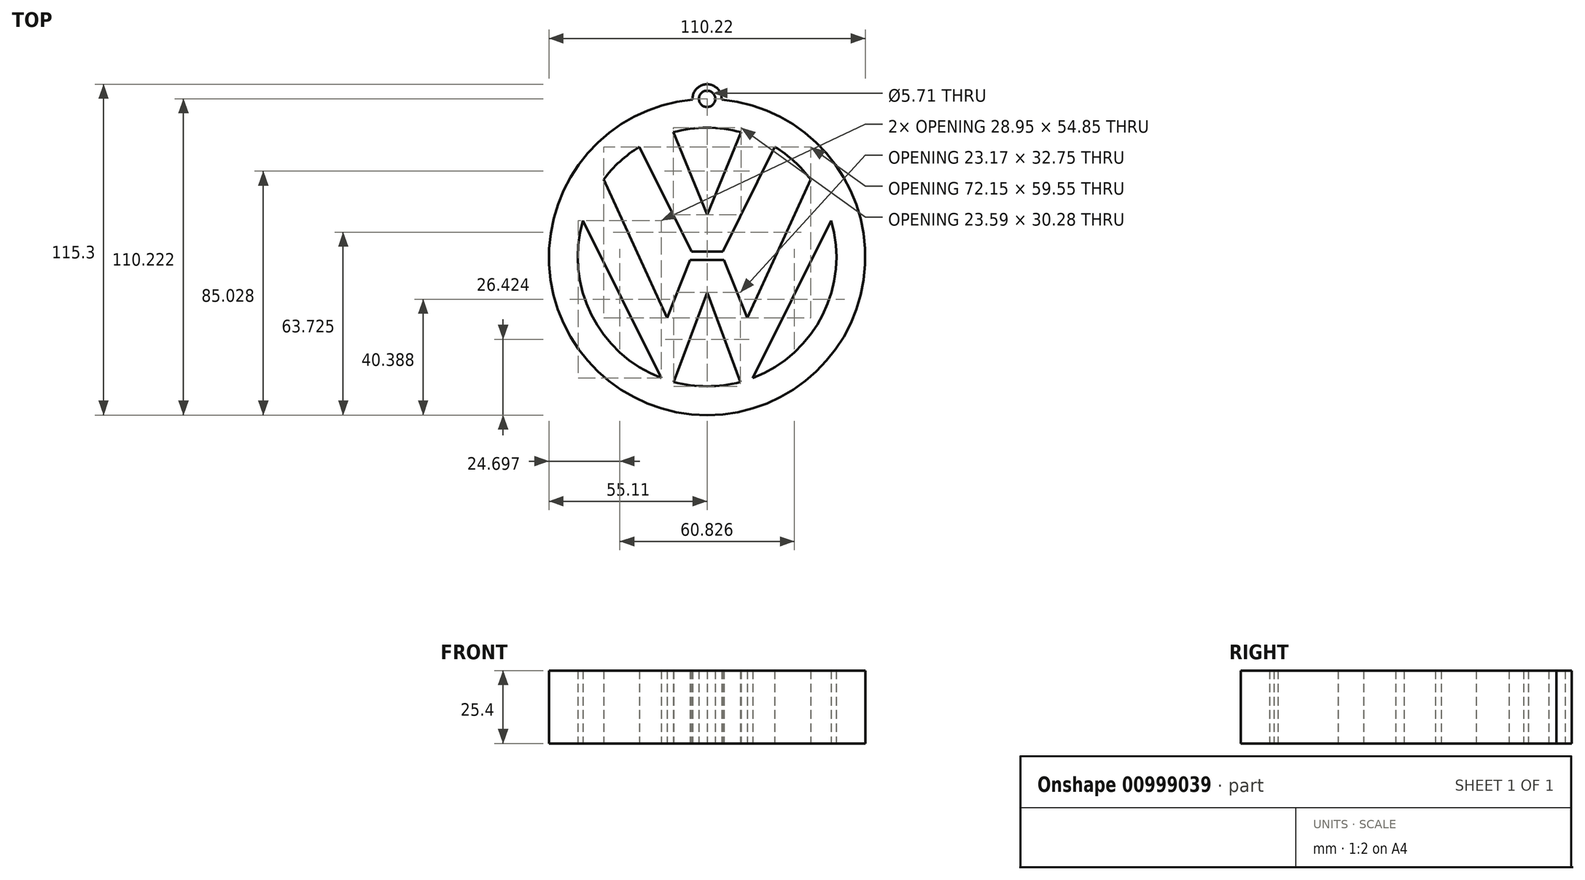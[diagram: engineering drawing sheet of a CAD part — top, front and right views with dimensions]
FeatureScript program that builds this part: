
annotation { "Feature Type Name" : "Feature", "Feature Type Description" : "" }
export const myFeature = defineFeature(function(context is Context, id is Id, definition is map)
    precondition{}
    {
        {
            var Q0;
            Q0=qCreatedBy(makeId("Top.planeOp"),FACE);
            var sketch = newSketch(context, id + "F0", { "sketchPlane" : qUnion([Q0])});
            skCircle(sketch, "E0", {"center": v(0, 0) * mm, "radius": 45.06 * mm});
            skArc(sketch, "E1", {"start": v(-5.07, 54.88) * mm, "mid": v(0, -55.11) * mm, "end": v(5.07, 54.88) * mm});
            skLineSegment(sketch, "E2", {"start": v(-11.8, 43.49) * mm, "end": v(0, 14.78) * mm});
            skLineSegment(sketch, "E3", {"start": v(0, 1.86) * mm, "end": v(-5.46, 1.86) * mm});
            skLineSegment(sketch, "E4", {"start": v(-5.46, 1.86) * mm, "end": v(-23.6, 38.4) * mm});
            skLineSegment(sketch, "E5", {"start": v(0, -12.31) * mm, "end": v(-11.58, -43.55) * mm});
            skLineSegment(sketch, "E6", {"start": v(-43.23, 12.7) * mm, "end": v(-15.94, -42.15) * mm});
            skLineSegment(sketch, "E7", {"start": v(-36.07, 27) * mm, "end": v(-13.96, -21.16) * mm});
            skLineSegment(sketch, "E8", {"start": v(-13.96, -21.16) * mm, "end": v(-5.88, -1.07) * mm});
            skLineSegment(sketch, "E9", {"start": v(-5.88, -1.07) * mm, "end": v(0, -1.07) * mm});
            skLineSegment(sketch, "E10.MirrorCS", {"start": v(11.8, 43.49) * mm, "end": v(0, 14.78) * mm});
            skLineSegment(sketch, "E11.MirrorCS", {"start": v(5.46, 1.86) * mm, "end": v(23.6, 38.4) * mm});
            skLineSegment(sketch, "E12.MirrorCS", {"start": v(0, 1.86) * mm, "end": v(5.46, 1.86) * mm});
            skLineSegment(sketch, "E13.MirrorCS", {"start": v(5.88, -1.07) * mm, "end": v(0, -1.07) * mm});
            skLineSegment(sketch, "E14.MirrorCS", {"start": v(0, -12.31) * mm, "end": v(11.58, -43.55) * mm});
            skLineSegment(sketch, "E15.MirrorCS", {"start": v(36.07, 27) * mm, "end": v(13.96, -21.16) * mm});
            skLineSegment(sketch, "E16.MirrorCS", {"start": v(43.23, 12.7) * mm, "end": v(15.94, -42.15) * mm});
            skLineSegment(sketch, "E17.MirrorCS", {"start": v(13.96, -21.16) * mm, "end": v(5.88, -1.07) * mm});
            skArc(sketch, "E18", {"start": v(5.07, 54.88) * mm, "mid": v(0, 60.2) * mm, "end": v(-5.07, 54.88) * mm});
            skCircle(sketch, "E19", {"center": v(0, 55.11) * mm, "radius": 2.86 * mm});
            skSolve(sketch);
        }
        {
            var Q0;
            Q0 = qSketchRegion(id + "F0", true);
            var Q1;
            {var subQ0=sQuery(id+"F0.wireOp",EDGE,"E2");Q1=makeQuery(id+"F0.imprint","IMPRINT",FACE,{"disambiguationData":[TD([[makeQuery(id+"F0.imprint","IMPRINT",EDGE,{"derivedFrom":subQ0}),-1.0]])]});}
            var Q2;
            {var subQ1=sQuery(id+"F0.wireOp",EDGE,"E5");Q2=makeQuery(id+"F0.imprint","IMPRINT",FACE,{"disambiguationData":[TD([[makeQuery(id+"F0.imprint","IMPRINT",EDGE,{"derivedFrom":subQ1}),-1.0]])]});}
            extrude(context, id + "F1", {"entities" : qUnion([Q0, Q1, Q2]), "depth" : 25.4 * mm, "offsetDistance" : 25.4 * mm});
        }
    });
